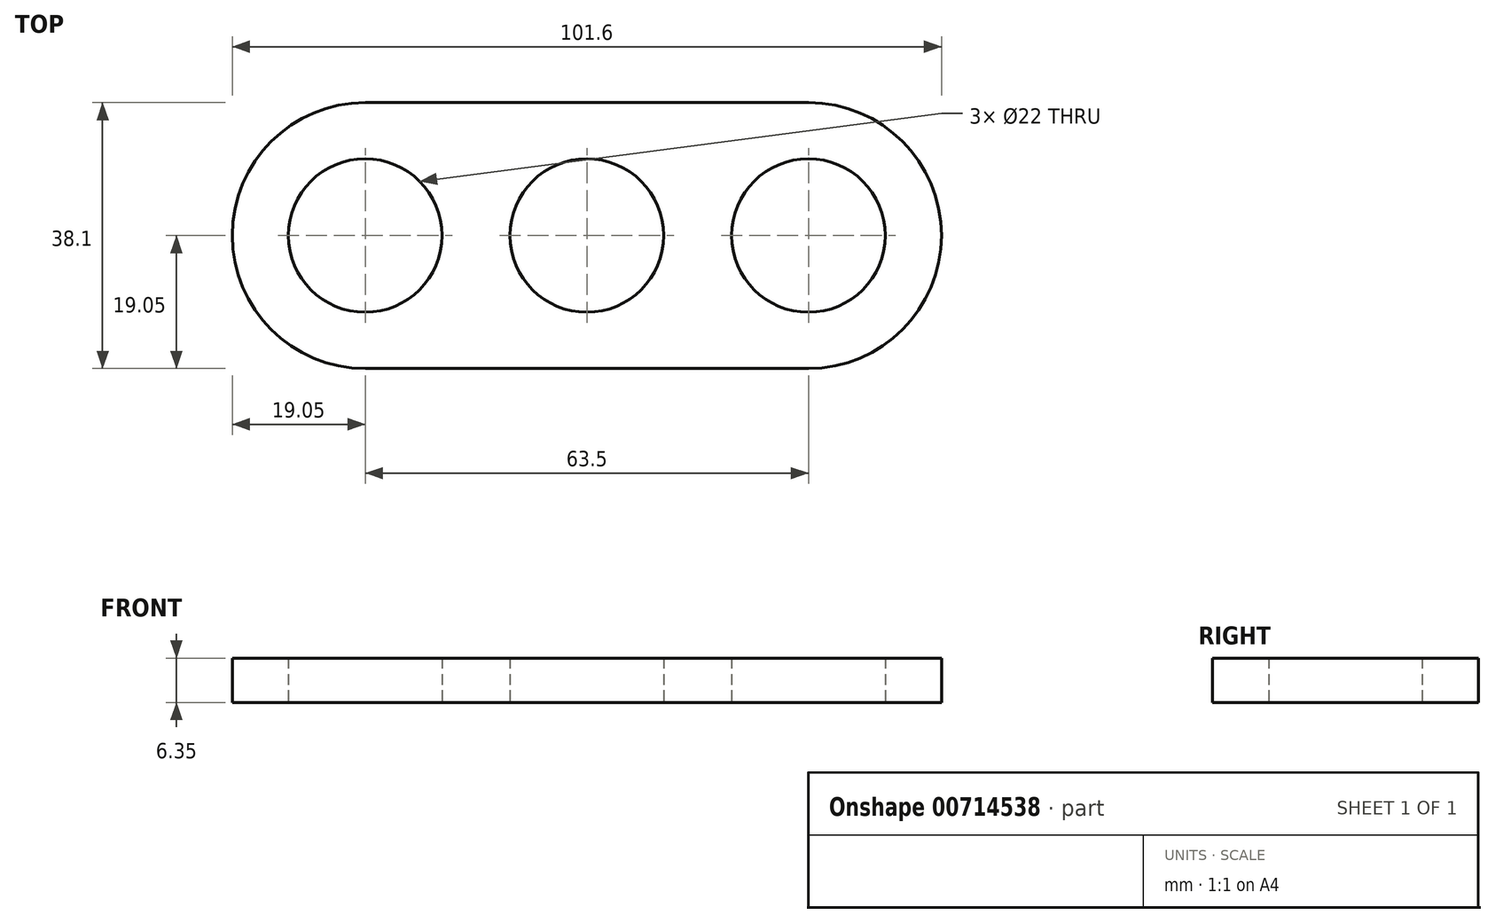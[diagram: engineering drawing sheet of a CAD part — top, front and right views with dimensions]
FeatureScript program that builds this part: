
annotation { "Feature Type Name" : "Feature", "Feature Type Description" : "" }
export const myFeature = defineFeature(function(context is Context, id is Id, definition is map)
    precondition{}
    {
        {
            var Q0;
            Q0=qCreatedBy(makeId("Top.planeOp"),FACE);
            var sketch = newSketch(context, id + "F0", { "sketchPlane" : qUnion([Q0])});
            skCircle(sketch, "E0", {"center": v(31.75, 0) * mm, "radius": 11 * mm});
            skCircle(sketch, "E1", {"center": v(0, 0) * mm, "radius": 11 * mm});
            skCircle(sketch, "E2", {"center": v(-31.75, 0) * mm, "radius": 11 * mm});
            skLineSegment(sketch, "E3", {"start": v(-31.75, 19.05) * mm, "end": v(31.75, 19.05) * mm});
            skLineSegment(sketch, "E4", {"start": v(-31.75, -19.05) * mm, "end": v(31.75, -19.05) * mm});
            skArc(sketch, "E5", {"start": v(31.75, -19.05) * mm, "mid": v(50.8, 0) * mm, "end": v(31.75, 19.05) * mm});
            skArc(sketch, "E6", {"start": v(-31.75, 19.05) * mm, "mid": v(-50.8, 0) * mm, "end": v(-31.75, -19.05) * mm});
            skSolve(sketch);
        }
        {
            var Q0;
            Q0=makeQuery(id+"F0.imprint","IMPRINT",FACE,{"disambiguationData":[TD([[makeQuery(id+"F0.imprint","IMPRINT",EDGE,{"derivedFrom":sQuery(id+"F0.wireOp",EDGE,"E1")}),-1.0]])]});
            extrude(context, id + "F1", {"entities" : qUnion([Q0]), "depth" : 6.35 * mm, "offsetDistance" : 25.4 * mm});
        }
    });
